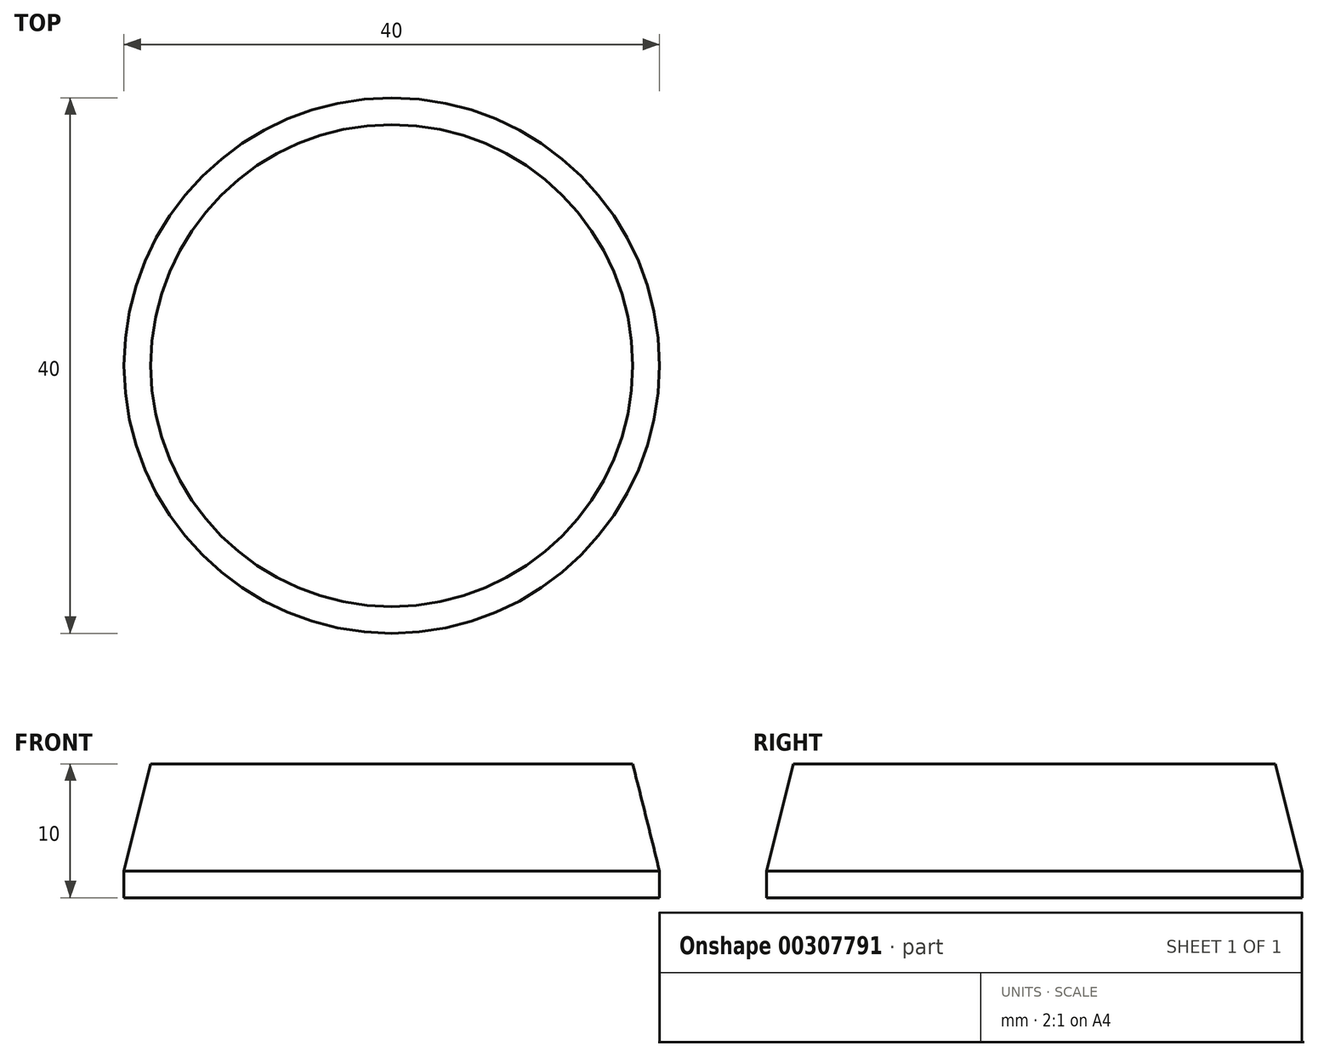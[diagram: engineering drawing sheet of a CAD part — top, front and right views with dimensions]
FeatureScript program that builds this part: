
annotation { "Feature Type Name" : "Feature", "Feature Type Description" : "" }
export const myFeature = defineFeature(function(context is Context, id is Id, definition is map)
    precondition{}
    {
        {
            var Q0;
            Q0=qCreatedBy(makeId("Top.planeOp"),FACE);
            var sketch = newSketch(context, id + "F0", { "sketchPlane" : qUnion([Q0])});
            skCircle(sketch, "E0", {"center": v(0, 0) * mm, "radius": 20 * mm});
            skSolve(sketch);
        }
        {
            var Q0;
            Q0=makeQuery(id+"F0.imprint","IMPRINT",FACE,{"disambiguationData":[TD([[makeQuery(id+"F0.imprint","IMPRINT",EDGE,{"derivedFrom":sQuery(id+"F0.wireOp",EDGE,"E0")}),1.0]])]});
            extrude(context, id + "F1", {"entities" : qUnion([Q0]), "depth" : 10 * mm});
        }
        {
            var Q0;
            Q0=makeQuery(id+"F1.opExtrude","CAP_EDGE",EDGE,{"disambiguationData":[OSD([sQuery(id+"F0.wireOp",EDGE,"E0")])],"isStart":false});
            chamfer(context, id + "F2", {"entities" : qUnion([Q0]), "chamferType" : ChamferType.TWO_OFFSETS, "width1" : 2 * mm, "oppositeDirection" : false, "width2" : 8 * mm, "tangentPropagation" : true});
        }
    });
